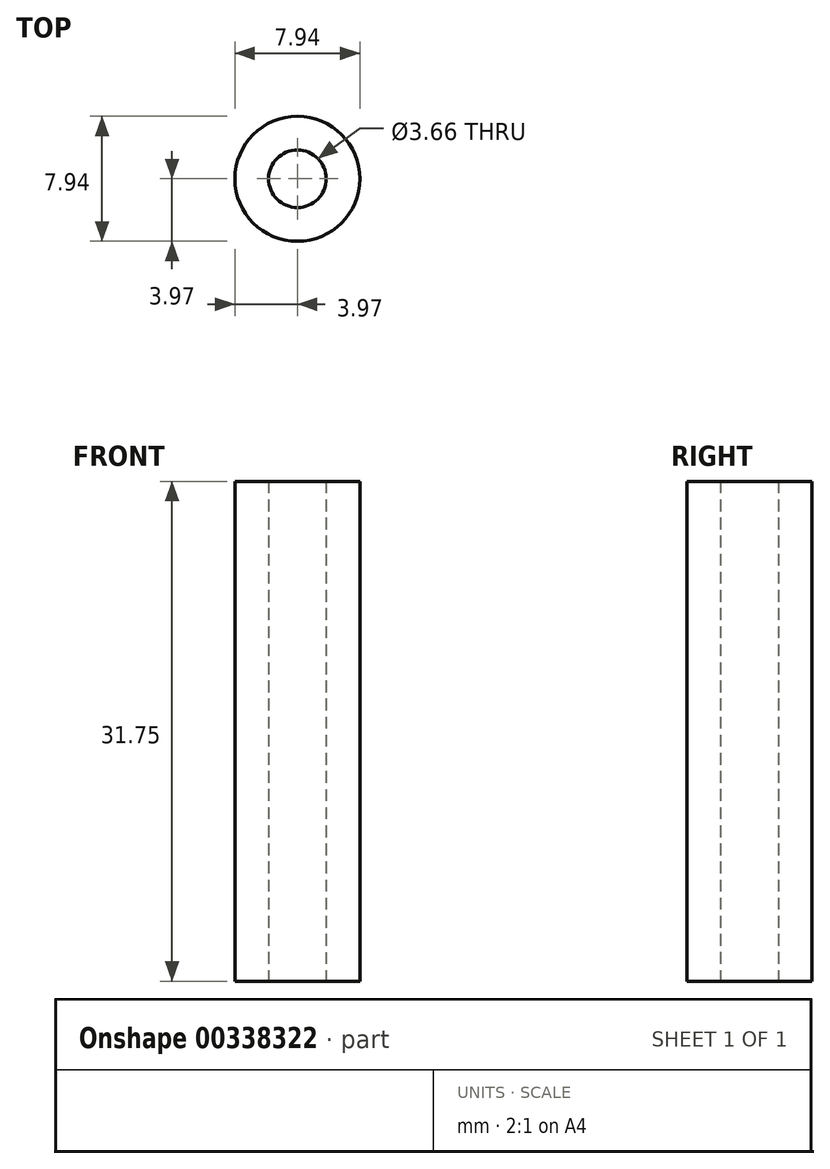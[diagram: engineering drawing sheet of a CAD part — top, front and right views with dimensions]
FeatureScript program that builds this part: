
annotation { "Feature Type Name" : "Feature", "Feature Type Description" : "" }
export const myFeature = defineFeature(function(context is Context, id is Id, definition is map)
    precondition{}
    {
        {
            var Q0;
            Q0=qCreatedBy(makeId("Top.planeOp"),FACE);
            var sketch = newSketch(context, id + "F0", { "sketchPlane" : qUnion([Q0])});
            skCircle(sketch, "E0", {"center": v(0, 0) * mm, "radius": 1.83 * mm});
            skCircle(sketch, "E1", {"center": v(0, 0) * mm, "radius": 3.97 * mm});
            skSolve(sketch);
        }
        {
            var Q0;
            Q0 = qSketchRegion(id + "F0", true);
            extrude(context, id + "F1", {"entities" : qUnion([Q0]), "depth" : 31.75 * mm});
        }
    });
